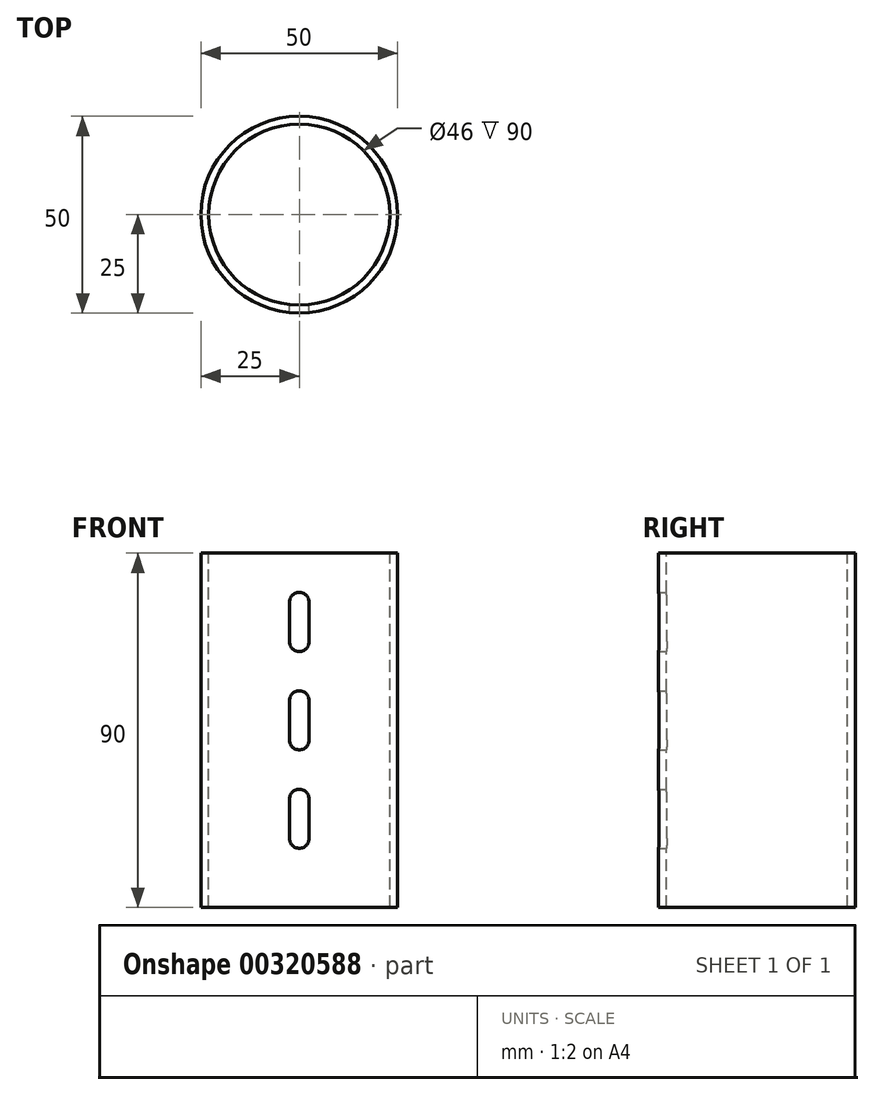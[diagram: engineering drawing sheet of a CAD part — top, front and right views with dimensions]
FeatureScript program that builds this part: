
annotation { "Feature Type Name" : "Feature", "Feature Type Description" : "" }
export const myFeature = defineFeature(function(context is Context, id is Id, definition is map)
    precondition{}
    {
        {
            var Q0;
            Q0=qCreatedBy(makeId("Front.planeOp"),FACE);
            var sketch = newSketch(context, id + "F0", { "sketchPlane" : qUnion([Q0])});
            skLineSegment(sketch, "E0.bottom", {"start": v(0, 45) * mm, "end": v(25, 45) * mm});
            skLineSegment(sketch, "E0.top", {"start": v(0, -45) * mm, "end": v(25, -45) * mm});
            skLineSegment(sketch, "E0.left", {"start": v(0, 45) * mm, "end": v(0, -45) * mm});
            skLineSegment(sketch, "E0.right", {"start": v(25, 45) * mm, "end": v(25, -45) * mm});
            skPoint(sketch, "E1", {"position": v(0, 0) * mm});
            skLineSegment(sketch, "E2", {"start": v(0, 64.55) * mm, "end": v(0, -57.15) * mm});
            skSolve(sketch);
        }
        {
            var Q0;
            {var subQ0=sQuery(id+"F0.wireOp",EDGE,"E0.bottom");Q0=makeQuery(id+"F0.imprint","IMPRINT",FACE,{"disambiguationData":[TD([[makeQuery(id+"F0.imprint","IMPRINT",EDGE,{"derivedFrom":subQ0}),-1.0]])]});}
            var Q1;
            Q1=sQuery(id+"F0.wireOp",EDGE,"E2");
            revolve(context, id + "F1", {"entities" : qUnion([Q0]), "axis" : qUnion([Q1]), "revolveType" : RevolveType.FULL});
        }
        {
            var Q0;
            Q0=makeQuery(id+"F1.opRevolve","SWEPT_FACE",FACE,{"disambiguationData":[OSD([sQuery(id+"F0.wireOp",EDGE,"E0.bottom")])]});
            var Q1;
            Q1=makeQuery(id+"F1.opRevolve","SWEPT_FACE",FACE,{"disambiguationData":[OSD([sQuery(id+"F0.wireOp",EDGE,"E0.top")])]});
            shell(context, id + "F2", {"entities" : qUnion([Q0, Q1]), "thickness" : 2 * mm});
        }
        {
            var Q0;
            Q0=qCreatedBy(makeId("Front.planeOp"),FACE);
            var sketch = newSketch(context, id + "F3", { "sketchPlane" : qUnion([Q0])});
            skLineSegment(sketch, "E3.left", {"start": v(-2.5, 32.5) * mm, "end": v(-2.5, 22.5) * mm});
            skLineSegment(sketch, "E3.right", {"start": v(2.5, 32.5) * mm, "end": v(2.5, 22.5) * mm});
            skPoint(sketch, "E4", {"position": v(0, 20) * mm});
            skArc(sketch, "E5", {"start": v(-2.5, 22.5) * mm, "mid": v(0, 20) * mm, "end": v(2.5, 22.5) * mm});
            skArc(sketch, "E6", {"start": v(2.5, 32.5) * mm, "mid": v(0, 35) * mm, "end": v(-2.5, 32.5) * mm});
            skPoint(sketch, "E7.orphan", {"position": v(2.5, 20) * mm});
            skPoint(sketch, "E8.orphan", {"position": v(-2.5, 20) * mm});
            skPoint(sketch, "E9", {"position": v(0, 35) * mm});
            skArc(sketch, "E10.0.1.0", {"start": v(-2.5, -2.5) * mm, "mid": v(0, -5) * mm, "end": v(2.5, -2.5) * mm});
            skLineSegment(sketch, "E10.0.1.1", {"start": v(2.5, 7.5) * mm, "end": v(2.5, -2.5) * mm});
            skLineSegment(sketch, "E10.0.1.2", {"start": v(-2.5, 7.5) * mm, "end": v(-2.5, -2.5) * mm});
            skArc(sketch, "E10.0.1.3", {"start": v(2.5, 7.5) * mm, "mid": v(0, 10) * mm, "end": v(-2.5, 7.5) * mm});
            skArc(sketch, "E10.0.2.0", {"start": v(-2.5, -27.5) * mm, "mid": v(0, -30) * mm, "end": v(2.5, -27.5) * mm});
            skLineSegment(sketch, "E10.0.2.1", {"start": v(2.5, -17.5) * mm, "end": v(2.5, -27.5) * mm});
            skLineSegment(sketch, "E10.0.2.2", {"start": v(-2.5, -17.5) * mm, "end": v(-2.5, -27.5) * mm});
            skArc(sketch, "E10.0.2.3", {"start": v(2.5, -17.5) * mm, "mid": v(0, -15) * mm, "end": v(-2.5, -17.5) * mm});
            skLineSegment(sketch, "E10.direction1", {"start": v(-2.5, 22.5) * mm, "end": v(22.5, 22.5) * mm, "construction": true});
            skLineSegment(sketch, "E10.direction2", {"start": v(-2.5, 22.5) * mm, "end": v(-2.5, -2.5) * mm, "construction": true});
            skSolve(sketch);
        }
        {
            var Q0;
            Q0 = qSketchRegion(id + "F3", true);
            extrude(context, id + "F4", {"entities" : qUnion([Q0]), "operationType" : NewBodyOperationType.REMOVE, "depth" : 84.2 * mm});
        }
    });
